# Revit family: Roof_Hydrant-Non_Freeze-Jay R.Smith-5907
name_source: partatom
category: Plumbing Fixtures
units: mm (PartAtom-declared; Revit-internal decimal feet)

## family parameters
Always vertical = Yes
Cut with Voids When Loaded = No
OmniClass Number = 23.65.70.11.11
OmniClass Title = Fixtures for Liquids
Part Type = Normal
Room Calculation Point = No
Round Connector Dimension = Use Diameter
Shared = No
Work Plane-Based = No

## types (1)
- 5907
    1/8" NPT Drain Hole = 1/8"
    3/4" Hose Connection = 3/4"
    Base Thickness = 2"
    CW Connection = Yes
    Connection Size = 3/4"
    Description = Roof Hydrant, non-freeze roof hydrant with galvanized casing and adjustable flow whieel lock handle with deck flange and under deck clamp.
    HW Connection = No
    Height = 53 1/2"
    Height from Metal Deck (Min. 17" - Max. 43") = 43"
    Manufacturer = J.R. Smith
    Material = Metal-Jay R. Smith-Galvanized Iron
    Model = 5907
    Product Documentation Link = https://www.jrsmith.com
    Product Page URL = https://www.jrsmith.com
    Product URL = http://www.jrsmith.com
    URL = http://www.jrsmith.com
    Vent Connection = No
    Waste Connection = Yes

## geometry (parser evidence)
native form markers: Sweep x5
no freeform markers — native parametric forms only
